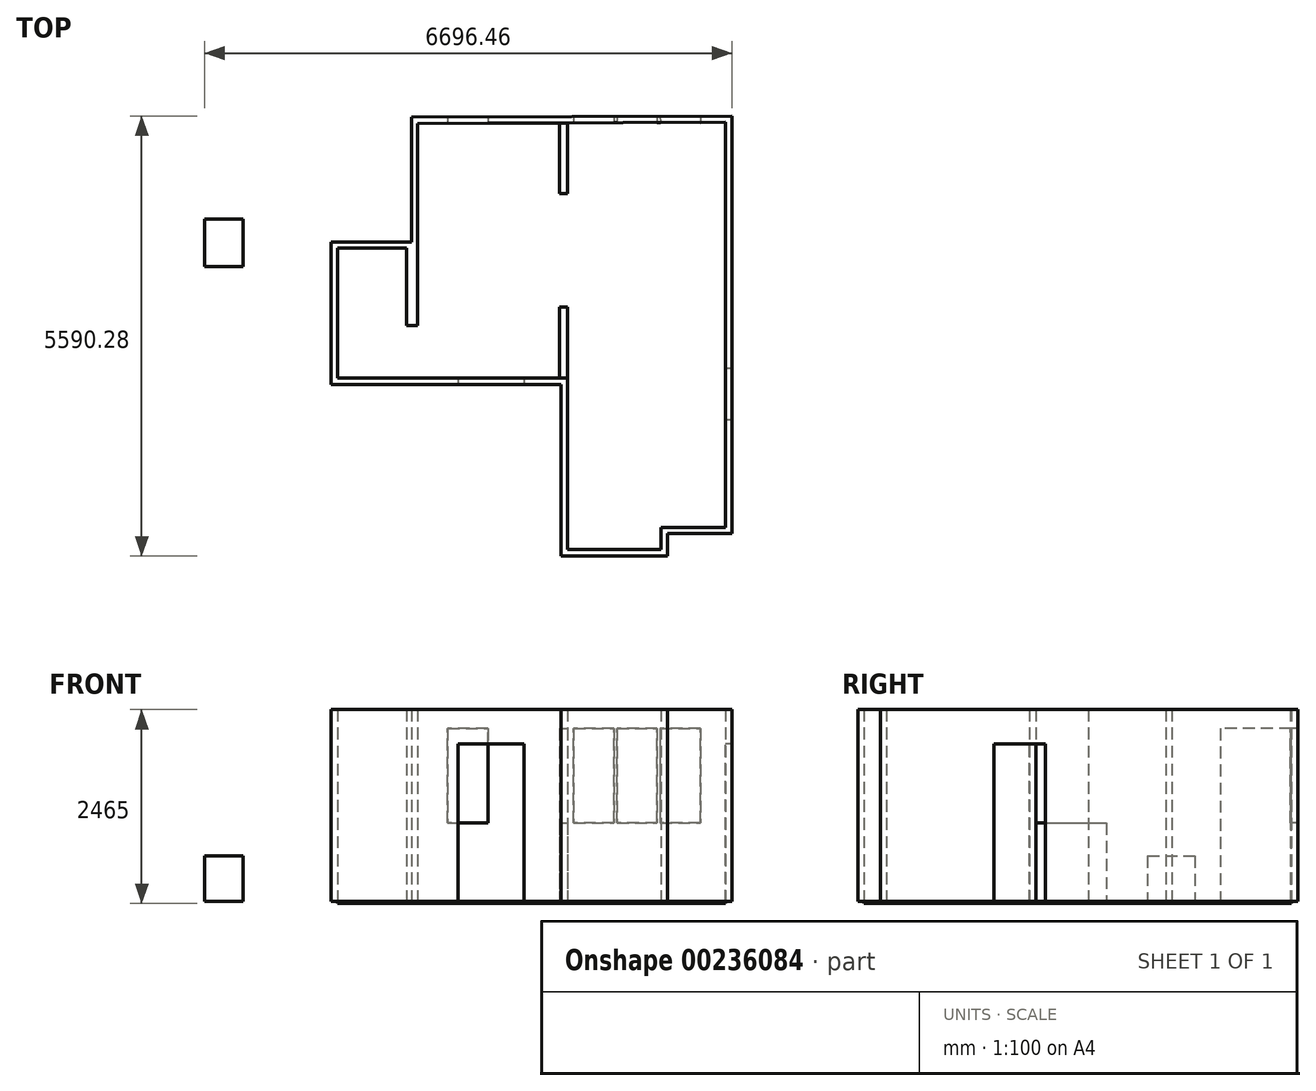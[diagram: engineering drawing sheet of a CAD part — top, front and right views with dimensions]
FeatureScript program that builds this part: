
annotation { "Feature Type Name" : "Feature", "Feature Type Description" : "" }
export const myFeature = defineFeature(function(context is Context, id is Id, definition is map)
    precondition{}
    {
        {
            var Q0;
            Q0=qCreatedBy(makeId("Top.planeOp"),FACE);
            var sketch = newSketch(context, id + "F0", { "sketchPlane" : qUnion([Q0])});
            skLineSegment(sketch, "E0", {"start": v(-1585, 134.86) * mm, "end": v(-1585, 1114.85) * mm});
            skLineSegment(sketch, "E1", {"start": v(-1585, 1114.85) * mm, "end": v(-2465, 1114.85) * mm});
            skLineSegment(sketch, "E2", {"start": v(-2465, 1114.85) * mm, "end": v(-2465, -535.14) * mm});
            skLineSegment(sketch, "E3", {"start": v(-2465, -535.14) * mm, "end": v(455, -535.14) * mm});
            skLineSegment(sketch, "E4", {"start": v(455, -535.14) * mm, "end": v(455, -2715.14) * mm});
            skLineSegment(sketch, "E5", {"start": v(455, -2715.14) * mm, "end": v(1645, -2715.14) * mm});
            skLineSegment(sketch, "E6", {"start": v(1645, -2715.14) * mm, "end": v(1645, -2430.14) * mm});
            skLineSegment(sketch, "E7", {"start": v(1645, -2430.14) * mm, "end": v(2465, -2430.14) * mm});
            skLineSegment(sketch, "E8", {"start": v(2465, -2430.14) * mm, "end": v(2465, 2714.85) * mm});
            skLineSegment(sketch, "E9", {"start": v(2465, 2714.85) * mm, "end": v(-1445, 2700.71) * mm});
            skLineSegment(sketch, "E10", {"start": v(-1445, 2700.71) * mm, "end": v(-1445, 134.86) * mm});
            skLineSegment(sketch, "E11", {"start": v(-1445, 134.86) * mm, "end": v(-1585, 134.86) * mm});
            skLineSegment(sketch, "E12", {"start": v(-1525, 1194.85) * mm, "end": v(-2545, 1194.85) * mm});
            skLineSegment(sketch, "E13", {"start": v(-2545, 1194.85) * mm, "end": v(-2545, -615.14) * mm});
            skLineSegment(sketch, "E14", {"start": v(-2545, -615.14) * mm, "end": v(375, -615.14) * mm});
            skLineSegment(sketch, "E15", {"start": v(375, -615.14) * mm, "end": v(375, -2795.14) * mm});
            skLineSegment(sketch, "E16", {"start": v(375, -2795.14) * mm, "end": v(1725, -2795.14) * mm});
            skLineSegment(sketch, "E17", {"start": v(1725, -2795.14) * mm, "end": v(1725, -2510.14) * mm});
            skLineSegment(sketch, "E18", {"start": v(1725, -2510.14) * mm, "end": v(2545, -2510.14) * mm});
            skLineSegment(sketch, "E19", {"start": v(2545, -2510.14) * mm, "end": v(2545, 2795.14) * mm});
            skLineSegment(sketch, "E20", {"start": v(2545, 2795.14) * mm, "end": v(-1525, 2780.42) * mm});
            skLineSegment(sketch, "E21", {"start": v(-1525, 2780.42) * mm, "end": v(-1525, 1194.85) * mm});
            skSolve(sketch);
        }
        {
            var Q0;
            Q0=makeQuery(id+"F0.imprint","IMPRINT",FACE,{"disambiguationData":[TD([[makeQuery(id+"F0.imprint","IMPRINT",EDGE,{"derivedFrom":sQuery(id+"F0.wireOp",EDGE,"E0")}),1.0]])]});
            extrude(context, id + "F1", {"entities" : qUnion([Q0]), "oppositeDirection" : true, "depth" : 25 * mm});
        }
        {
            var Q0;
            Q0 = qSketchRegion(id + "F0", true);
            extrude(context, id + "F2", {"entities" : qUnion([Q0]), "depth" : 2440 * mm});
        }
        {
            var Q0;
            Q0=makeQuery(id+"F2.opExtrude","SWEPT_FACE",FACE,{"disambiguationData":[OSD([sQuery(id+"F0.wireOp",EDGE,"E14")])]});
            var sketch = newSketch(context, id + "F3", { "sketchPlane" : qUnion([Q0])});
            skLineSegment(sketch, "E22.bottom", {"start": v(-935, 0) * mm, "end": v(-95, 0) * mm});
            skLineSegment(sketch, "E22.top", {"start": v(-935, 2000) * mm, "end": v(-95, 2000) * mm});
            skLineSegment(sketch, "E22.left", {"start": v(-935, 0) * mm, "end": v(-935, 2000) * mm});
            skLineSegment(sketch, "E22.right", {"start": v(-95, 0) * mm, "end": v(-95, 2000) * mm});
            skSolve(sketch);
        }
        {
            var Q0;
            Q0=makeQuery(id+"F3.imprint","IMPRINT",FACE,{"disambiguationData":[TD([[makeQuery(id+"F3.imprint","IMPRINT",EDGE,{"derivedFrom":sQuery(id+"F3.wireOp",EDGE,"E22.bottom")}),1.0]])]});
            extrude(context, id + "F4", {"entities" : qUnion([Q0]), "operationType" : NewBodyOperationType.REMOVE, "endBound" : BoundingType.UP_TO_NEXT, "oppositeDirection" : true, "depth" : 25 * mm});
        }
        {
            var Q0;
            Q0=makeQuery(id+"F1.opExtrude","CAP_FACE",FACE,{"disambiguationData":[OSD([sQuery(id+"F0.wireOp",EDGE,"E0"),sQuery(id+"F0.wireOp",EDGE,"E1"),sQuery(id+"F0.wireOp",EDGE,"E2"),sQuery(id+"F0.wireOp",EDGE,"E3"),sQuery(id+"F0.wireOp",EDGE,"E4"),sQuery(id+"F0.wireOp",EDGE,"E5"),sQuery(id+"F0.wireOp",EDGE,"E6"),sQuery(id+"F0.wireOp",EDGE,"E7"),sQuery(id+"F0.wireOp",EDGE,"E8"),sQuery(id+"F0.wireOp",EDGE,"E9"),sQuery(id+"F0.wireOp",EDGE,"E10"),sQuery(id+"F0.wireOp",EDGE,"E11")])],"isStart":true});
            var sketch = newSketch(context, id + "F5", { "sketchPlane" : qUnion([Q0])});
            skLineSegment(sketch, "E23.bottom", {"start": v(355, 2707.22) * mm, "end": v(455, 2707.22) * mm});
            skLineSegment(sketch, "E23.top", {"start": v(355, 1807.22) * mm, "end": v(455, 1807.22) * mm});
            skLineSegment(sketch, "E23.left", {"start": v(355, 2707.22) * mm, "end": v(355, 1807.22) * mm});
            skLineSegment(sketch, "E23.right", {"start": v(455, 2707.22) * mm, "end": v(455, 1807.22) * mm});
            skLineSegment(sketch, "E24.bottom", {"start": v(455, -535.14) * mm, "end": v(355, -535.14) * mm});
            skSolve(sketch);
        }
        {
            var Q0;
            Q0=makeQuery(id+"F5.imprint","IMPRINT",FACE,{"disambiguationData":[TD([[makeQuery(id+"F5.imprint","IMPRINT",EDGE,{"derivedFrom":sQuery(id+"F5.wireOp",EDGE,"E23.bottom")}),-1.0]])]});
            extrude(context, id + "F6", {"entities" : qUnion([Q0]), "operationType" : NewBodyOperationType.ADD, "depth" : 2200 * mm});
        }
        {
            var Q0;
            Q0=makeQuery(id+"F1.opExtrude","CAP_FACE",FACE,{"disambiguationData":[OSD([sQuery(id+"F0.wireOp",EDGE,"E0"),sQuery(id+"F0.wireOp",EDGE,"E1"),sQuery(id+"F0.wireOp",EDGE,"E2"),sQuery(id+"F0.wireOp",EDGE,"E3"),sQuery(id+"F0.wireOp",EDGE,"E4"),sQuery(id+"F0.wireOp",EDGE,"E5"),sQuery(id+"F0.wireOp",EDGE,"E6"),sQuery(id+"F0.wireOp",EDGE,"E7"),sQuery(id+"F0.wireOp",EDGE,"E8"),sQuery(id+"F0.wireOp",EDGE,"E9"),sQuery(id+"F0.wireOp",EDGE,"E10"),sQuery(id+"F0.wireOp",EDGE,"E11")])],"isStart":true});
            var sketch = newSketch(context, id + "F7", { "sketchPlane" : qUnion([Q0])});
            skLineSegment(sketch, "E25.bottom", {"start": v(455, -535.14) * mm, "end": v(355, -535.14) * mm});
            skLineSegment(sketch, "E25.top", {"start": v(455, 364.86) * mm, "end": v(355, 364.86) * mm});
            skLineSegment(sketch, "E25.left", {"start": v(455, -535.14) * mm, "end": v(455, 364.86) * mm});
            skLineSegment(sketch, "E25.right", {"start": v(355, -535.14) * mm, "end": v(355, 364.86) * mm});
            skSolve(sketch);
        }
        {
            var Q0;
            Q0=makeQuery(id+"F7.imprint","IMPRINT",FACE,{"disambiguationData":[TD([[makeQuery(id+"F7.imprint","IMPRINT",EDGE,{"derivedFrom":sQuery(id+"F7.wireOp",EDGE,"E25.bottom")}),1.0]])]});
            extrude(context, id + "F8", {"entities" : qUnion([Q0]), "depth" : 1000 * mm});
        }
        {
            var Q0;
            Q0=makeQuery(id+"F2.opExtrude","SWEPT_FACE",FACE,{"disambiguationData":[OSD([sQuery(id+"F0.wireOp",EDGE,"E9")])]});
            var sketch = newSketch(context, id + "F9", { "sketchPlane" : qUnion([Q0])});
            skLineSegment(sketch, "E26.bottom", {"start": v(-1055.22, 1000) * mm, "end": v(-545.22, 1000) * mm});
            skLineSegment(sketch, "E26.top", {"start": v(-1055.22, 2200) * mm, "end": v(-545.22, 2200) * mm});
            skLineSegment(sketch, "E26.left", {"start": v(-1055.22, 1000) * mm, "end": v(-1055.22, 2200) * mm});
            skLineSegment(sketch, "E26.right", {"start": v(-545.22, 1000) * mm, "end": v(-545.22, 2200) * mm});
            skLineSegment(sketch, "E27.bottom", {"start": v(544.8, 1000) * mm, "end": v(1054.8, 1000) * mm});
            skLineSegment(sketch, "E27.top", {"start": v(544.8, 2200) * mm, "end": v(1054.8, 2200) * mm});
            skLineSegment(sketch, "E27.left", {"start": v(544.8, 1000) * mm, "end": v(544.8, 2200) * mm});
            skLineSegment(sketch, "E27.right", {"start": v(1054.8, 1000) * mm, "end": v(1054.8, 2200) * mm});
            skPoint(sketch, "E28.firstSnap0", {"position": v(1181.99, 1010.53) * mm});
            skLineSegment(sketch, "E29.bottom", {"start": v(1094.8, 1000) * mm, "end": v(1604.8, 1000) * mm});
            skLineSegment(sketch, "E29.top", {"start": v(1094.8, 2200) * mm, "end": v(1604.8, 2200) * mm});
            skLineSegment(sketch, "E29.left", {"start": v(1094.8, 1000) * mm, "end": v(1094.8, 2200) * mm});
            skLineSegment(sketch, "E29.right", {"start": v(1604.8, 1000) * mm, "end": v(1604.8, 2200) * mm});
            skLineSegment(sketch, "E30.bottom", {"start": v(1644.8, 1000) * mm, "end": v(2154.8, 1000) * mm});
            skLineSegment(sketch, "E30.top", {"start": v(1644.8, 2200) * mm, "end": v(2154.8, 2200) * mm});
            skLineSegment(sketch, "E30.left", {"start": v(1644.8, 1000) * mm, "end": v(1644.8, 2200) * mm});
            skLineSegment(sketch, "E30.right", {"start": v(2154.8, 1000) * mm, "end": v(2154.8, 2200) * mm});
            skSolve(sketch);
        }
        {
            var Q0;
            Q0=makeQuery(id+"F9.imprint","IMPRINT",FACE,{"disambiguationData":[TD([[makeQuery(id+"F9.imprint","IMPRINT",EDGE,{"derivedFrom":sQuery(id+"F9.wireOp",EDGE,"E27.bottom")}),1.0]])]});
            var Q1;
            Q1=makeQuery(id+"F9.imprint","IMPRINT",FACE,{"disambiguationData":[TD([[makeQuery(id+"F9.imprint","IMPRINT",EDGE,{"derivedFrom":sQuery(id+"F9.wireOp",EDGE,"E26.bottom")}),1.0]])]});
            var Q2;
            Q2=makeQuery(id+"F9.imprint","IMPRINT",FACE,{"disambiguationData":[TD([[makeQuery(id+"F9.imprint","IMPRINT",EDGE,{"derivedFrom":sQuery(id+"F9.wireOp",EDGE,"E30.bottom")}),1.0]])]});
            var Q3;
            Q3=makeQuery(id+"F9.imprint","IMPRINT",FACE,{"disambiguationData":[TD([[makeQuery(id+"F9.imprint","IMPRINT",EDGE,{"derivedFrom":sQuery(id+"F9.wireOp",EDGE,"E29.bottom")}),1.0]])]});
            extrude(context, id + "F10", {"entities" : qUnion([Q0, Q1, Q2, Q3]), "operationType" : NewBodyOperationType.REMOVE, "endBound" : BoundingType.UP_TO_NEXT, "oppositeDirection" : true, "depth" : 25 * mm});
        }
        {
            var Q0;
            Q0=makeQuery(id+"F1.opExtrude","CAP_FACE",FACE,{"disambiguationData":[OSD([sQuery(id+"F0.wireOp",EDGE,"E0"),sQuery(id+"F0.wireOp",EDGE,"E1"),sQuery(id+"F0.wireOp",EDGE,"E2"),sQuery(id+"F0.wireOp",EDGE,"E3"),sQuery(id+"F0.wireOp",EDGE,"E4"),sQuery(id+"F0.wireOp",EDGE,"E5"),sQuery(id+"F0.wireOp",EDGE,"E6"),sQuery(id+"F0.wireOp",EDGE,"E7"),sQuery(id+"F0.wireOp",EDGE,"E8"),sQuery(id+"F0.wireOp",EDGE,"E9"),sQuery(id+"F0.wireOp",EDGE,"E10"),sQuery(id+"F0.wireOp",EDGE,"E11")])],"isStart":true});
            var sketch = newSketch(context, id + "F11", { "sketchPlane" : qUnion([Q0])});
            skLineSegment(sketch, "E31.bottom", {"start": v(-4151.46, 883) * mm, "end": v(-3661.46, 883) * mm});
            skLineSegment(sketch, "E31.top", {"start": v(-4151.46, 1483) * mm, "end": v(-3661.46, 1483) * mm});
            skLineSegment(sketch, "E31.left", {"start": v(-4151.46, 883) * mm, "end": v(-4151.46, 1483) * mm});
            skLineSegment(sketch, "E31.right", {"start": v(-3661.46, 883) * mm, "end": v(-3661.46, 1483) * mm});
            skSolve(sketch);
        }
        {
            var Q0;
            Q0 = qSketchRegion(id + "F11", true);
            extrude(context, id + "F12", {"entities" : qUnion([Q0]), "depth" : 580 * mm});
        }
        {
            var Q0;
            Q0=makeQuery(id+"F2.opExtrude","SWEPT_FACE",FACE,{"disambiguationData":[OSD([sQuery(id+"F0.wireOp",EDGE,"E8")])]});
            var sketch = newSketch(context, id + "F13", { "sketchPlane" : qUnion([Q0])});
            skLineSegment(sketch, "E32.bottom", {"start": v(415.15, 0) * mm, "end": v(1065.15, 0) * mm});
            skLineSegment(sketch, "E32.top", {"start": v(415.15, 2000) * mm, "end": v(1065.15, 2000) * mm});
            skLineSegment(sketch, "E32.left", {"start": v(1065.15, 0) * mm, "end": v(1065.15, 2000) * mm});
            skLineSegment(sketch, "E32.right", {"start": v(415.15, 0) * mm, "end": v(415.15, 2000) * mm});
            skSolve(sketch);
        }
        {
            var Q0;
            Q0 = qSketchRegion(id + "F13", true);
            extrude(context, id + "F14", {"entities" : qUnion([Q0]), "operationType" : NewBodyOperationType.REMOVE, "endBound" : BoundingType.UP_TO_NEXT, "oppositeDirection" : true, "depth" : 25 * mm});
        }
    });
